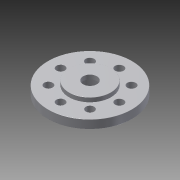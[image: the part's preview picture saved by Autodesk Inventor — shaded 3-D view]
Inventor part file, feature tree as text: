
AUTODESK INVENTOR PART (.ipt)
format: ipt  version: 2013 (Build 170138000, 138)  size: 186,368 bytes
history: native  units: mm
features: sketch x6, extrude x4, hole x2, other x1, pattern_circular x1, fillet x1
ambient origin geometry x1: Origin
feature tree (15):
  other  "ソリッド1"
  extrude  "押し出し1"  Depth=20.0mm
  extrude  "押し出し2"  Depth=2.0mm TaperAngle=0.0deg
  extrude  "押し出し3"  Depth=10.0mm
  extrude  "押し出し4"  Depth=1.0mm TaperAngle=0.0deg
  hole  "穴1"  [1 undecoded]
  hole  "穴2"  [1 undecoded]
  pattern_circular  "円形状パターン1"  [2 undecoded]
  fillet  "フィレット3"  Radius=3.0mm
  sketch  "スケッチ1"
  sketch  "スケッチ2"
  sketch  "スケッチ4"
  sketch  "スケッチ5"
  sketch  "スケッチ6"
  sketch  "スケッチ7"
note: 4 required parameter values undecoded (feature->parameter linkage not recoverable at this tier; creation-order binding heuristic only, values carry confidence <= 0.55)
